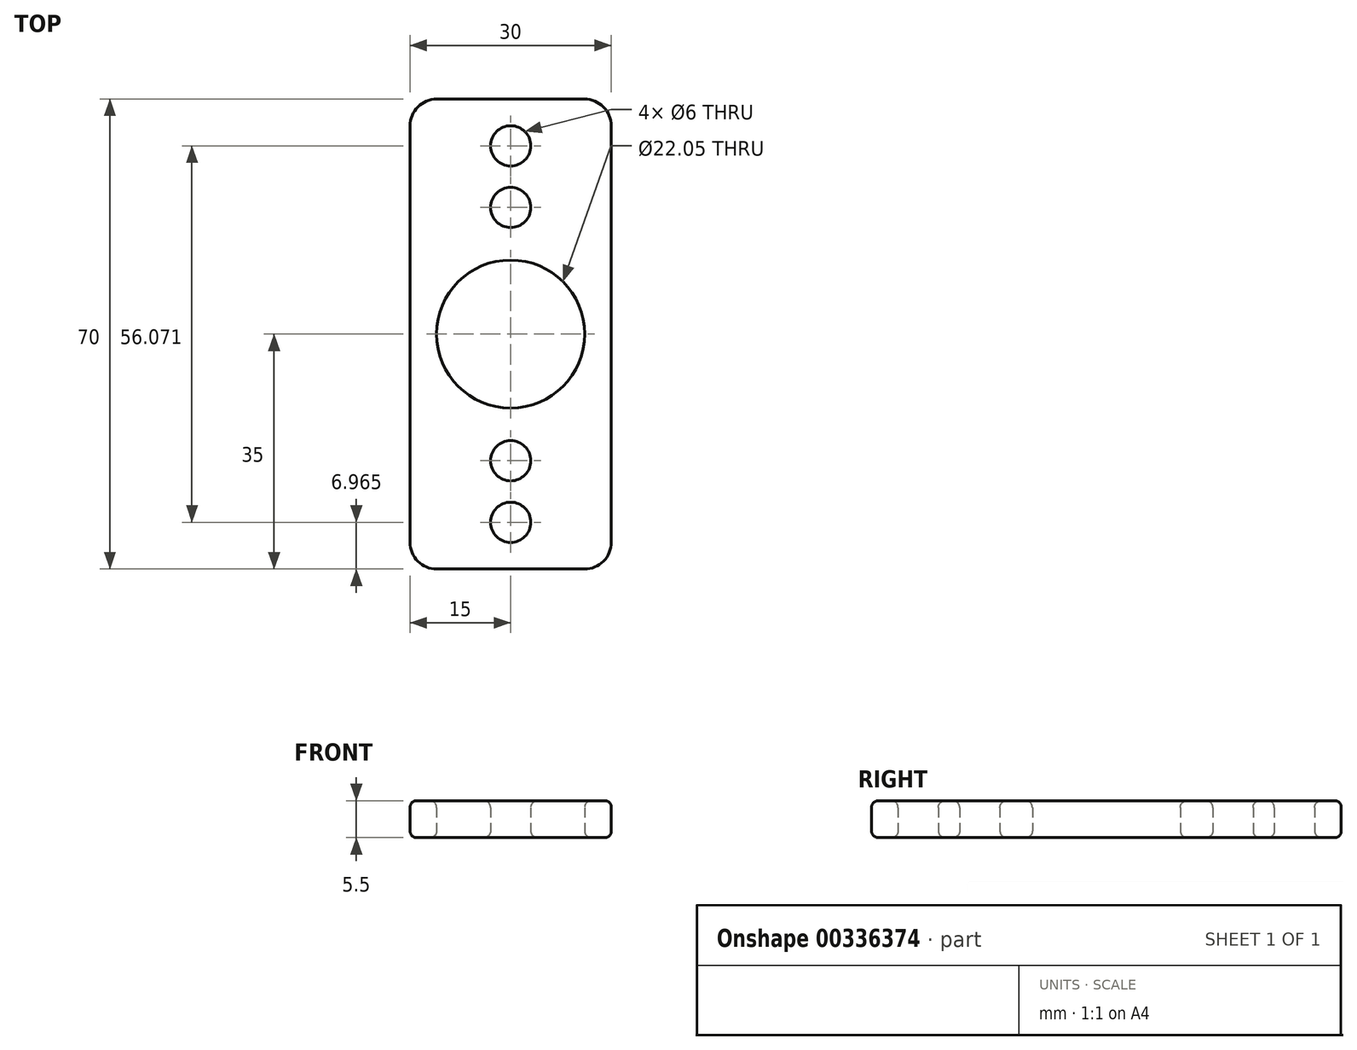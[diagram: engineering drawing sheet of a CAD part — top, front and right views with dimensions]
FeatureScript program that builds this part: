
annotation { "Feature Type Name" : "Feature", "Feature Type Description" : "" }
export const myFeature = defineFeature(function(context is Context, id is Id, definition is map)
    precondition{}
    {
        {
            var Q0;
            Q0=qCreatedBy(makeId("Top.planeOp"),FACE);
            var sketch = newSketch(context, id + "F0", { "sketchPlane" : qUnion([Q0])});
            skLineSegment(sketch, "E0.bottom", {"start": v(15, 35) * mm, "end": v(-15, 35) * mm});
            skLineSegment(sketch, "E0.top", {"start": v(15, -35) * mm, "end": v(-15, -35) * mm});
            skLineSegment(sketch, "E0.left", {"start": v(15, 35) * mm, "end": v(15, -35) * mm});
            skLineSegment(sketch, "E0.right", {"start": v(-15, 35) * mm, "end": v(-15, -35) * mm});
            skPoint(sketch, "E0.middle", {"position": v(0, 0) * mm});
            skCircle(sketch, "E1", {"center": v(0, 0) * mm, "radius": 11.03 * mm});
            skCircle(sketch, "E2", {"center": v(0, 28.04) * mm, "radius": 3 * mm});
            skCircle(sketch, "E3", {"center": v(0, 18.86) * mm, "radius": 3 * mm});
            skCircle(sketch, "E4.MirrorC", {"center": v(0, -18.86) * mm, "radius": 3 * mm});
            skCircle(sketch, "E5.MirrorC", {"center": v(0, -28.04) * mm, "radius": 3 * mm});
            skSolve(sketch);
        }
        {
            var Q0;
            Q0=makeQuery(id+"F0.imprint","IMPRINT",FACE,{"disambiguationData":[TD([[makeQuery(id+"F0.imprint","IMPRINT",EDGE,{"derivedFrom":sQuery(id+"F0.wireOp",EDGE,"E0.bottom")}),1.0]])]});
            extrude(context, id + "F1", {"entities" : qUnion([Q0]), "depth" : 5.5 * mm, "offsetDistance" : 25 * mm});
        }
        {
            var Q0;
            Q0=makeQuery(id+"F1.opExtrude","CAP_FACE",FACE,{"disambiguationData":[OSD([sQuery(id+"F0.wireOp",EDGE,"E0.bottom"),sQuery(id+"F0.wireOp",EDGE,"E0.top"),sQuery(id+"F0.wireOp",EDGE,"E0.left"),sQuery(id+"F0.wireOp",EDGE,"E0.right"),sQuery(id+"F0.wireOp",EDGE,"E1"),sQuery(id+"F0.wireOp",EDGE,"vHjHliSe-Skoh-hfip-g2Oa-lgDYq0DfT5FR"),sQuery(id+"F0.wireOp",EDGE,"c646de05-a651-48e9-a651-e3e6a16a325d0.MirrorC")])],"isStart":false});
            var Q1;
            Q1=makeQuery(id+"F1.opExtrude","CAP_FACE",FACE,{"disambiguationData":[OSD([sQuery(id+"F0.wireOp",EDGE,"E0.bottom"),sQuery(id+"F0.wireOp",EDGE,"E0.top"),sQuery(id+"F0.wireOp",EDGE,"E0.left"),sQuery(id+"F0.wireOp",EDGE,"E0.right"),sQuery(id+"F0.wireOp",EDGE,"E1"),sQuery(id+"F0.wireOp",EDGE,"vHjHliSe-Skoh-hfip-g2Oa-lgDYq0DfT5FR"),sQuery(id+"F0.wireOp",EDGE,"c646de05-a651-48e9-a651-e3e6a16a325d0.MirrorC")])],"isStart":true});
            fillet(context, id + "F2", {"entities" : qUnion([Q0, Q1]), "tangentPropagation" : true, "radius" : 1 * mm, "defaultsChanged" : true, "vertexSettings" : [], "allowEdgeOverflow" : false});
        }
        {
            var Q0;
            Q0=makeQuery(id+"F1.opExtrude","SWEPT_EDGE",EDGE,{"disambiguationData":[OSD([sQuery(id+"F0.wireOp",EDGE,"E0.top"),sQuery(id+"F0.wireOp",EDGE,"E0.right")])]});
            var Q1;
            Q1=makeQuery(id+"F1.opExtrude","SWEPT_EDGE",EDGE,{"disambiguationData":[OSD([sQuery(id+"F0.wireOp",EDGE,"E0.top"),sQuery(id+"F0.wireOp",EDGE,"E0.left")])]});
            var Q2;
            Q2=makeQuery(id+"F1.opExtrude","SWEPT_EDGE",EDGE,{"disambiguationData":[OSD([sQuery(id+"F0.wireOp",EDGE,"E0.bottom"),sQuery(id+"F0.wireOp",EDGE,"E0.left")])]});
            var Q3;
            Q3=makeQuery(id+"F1.opExtrude","SWEPT_EDGE",EDGE,{"disambiguationData":[OSD([sQuery(id+"F0.wireOp",EDGE,"E0.bottom"),sQuery(id+"F0.wireOp",EDGE,"E0.right")])]});
            fillet(context, id + "F3", {"entities" : qUnion([Q0, Q1, Q2, Q3]), "tangentPropagation" : true, "radius" : 4 * mm, "defaultsChanged" : false, "vertexSettings" : [], "allowEdgeOverflow" : false});
        }
    });
